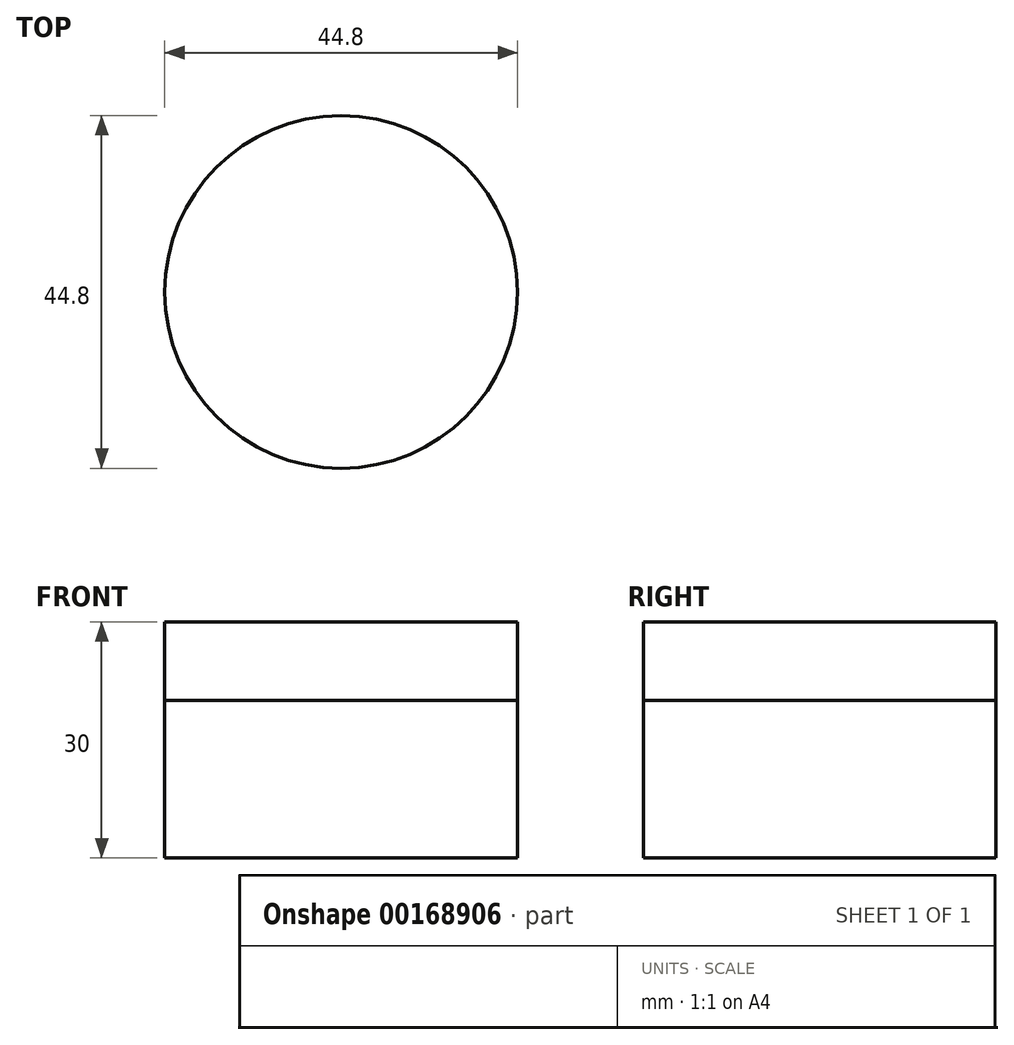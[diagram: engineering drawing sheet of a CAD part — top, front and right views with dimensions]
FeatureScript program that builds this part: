
annotation { "Feature Type Name" : "Feature", "Feature Type Description" : "" }
export const myFeature = defineFeature(function(context is Context, id is Id, definition is map)
    precondition{}
    {
        {
            var Q0;
            Q0=qCreatedBy(makeId("Top.planeOp"),FACE);
            var sketch = newSketch(context, id + "F0", { "sketchPlane" : qUnion([Q0])});
            skCircle(sketch, "E0", {"center": v(0, 0) * mm, "radius": 22.4 * mm});
            skSolve(sketch);
        }
        {
            var Q0;
            Q0 = qSketchRegion(id + "F0", true);
            extrude(context, id + "F1", {"entities" : qUnion([Q0]), "depth" : 20 * mm});
        }
        {
            var Q0;
            Q0=makeQuery(id+"F1.opExtrude","CAP_FACE",FACE,{"disambiguationData":[OSD([sQuery(id+"F0.wireOp",EDGE,"E0")])],"isStart":false});
            extrude(context, id + "F2", {"entities" : qUnion([Q0]), "depth" : 10 * mm});
        }
    });
